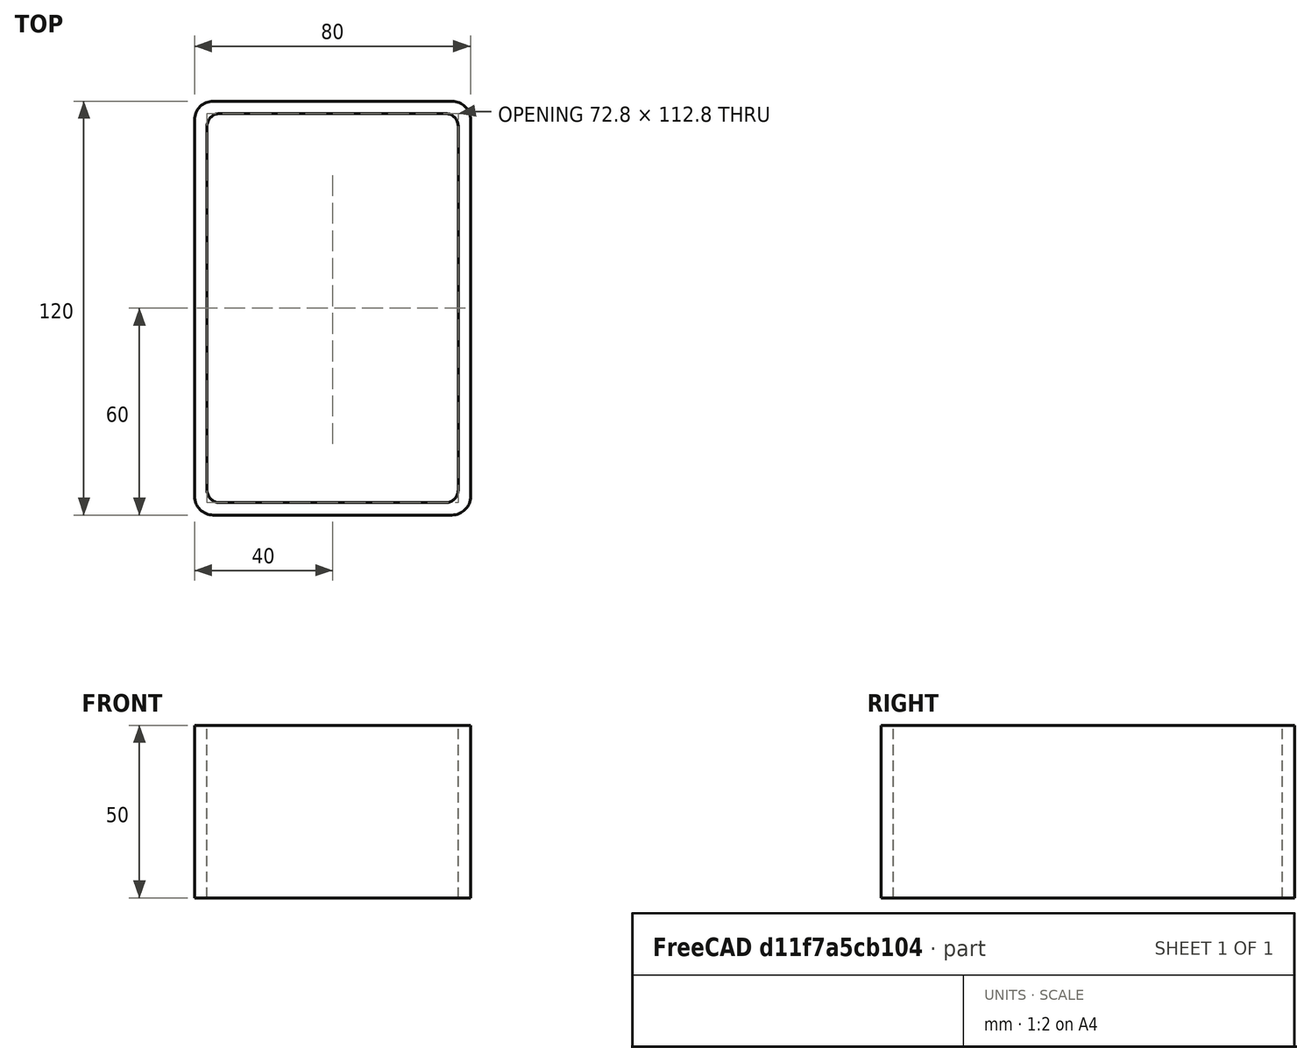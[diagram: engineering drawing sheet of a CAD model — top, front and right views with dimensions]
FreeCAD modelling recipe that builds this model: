
FCSTD DOCUMENT  (FreeCAD 0.15R4671 (Git))
Label: Rectangular hollow section 120x80x3.6 EN10219 S235JRH
License: All rights reserved
LicenseURL: http://en.wikipedia.org/wiki/All_rights_reserved
objects: Sketcher::SketchObject×1, Part::Extrusion×1
note: 2 computed .brp shape members not serialized (recipe doc carries the construction recipe); baked Part::Feature solids carry a one-line shape summary decoded from their .brp

FEATURE [Sketcher::SketchObject] Sketch
  sketch-geometry (16):
    g0: LineSegment StartX=-32.8 StartY=56.4 StartZ=0 EndX=32.8 EndY=56.4 EndZ=0
    g1: LineSegment StartX=36.4 StartY=52.8 StartZ=0 EndX=36.4 EndY=-52.8 EndZ=0
    g2: LineSegment StartX=32.8 StartY=-56.4 StartZ=0 EndX=-32.8 EndY=-56.4 EndZ=0
    g3: LineSegment StartX=-36.4 StartY=-52.8 StartZ=0 EndX=-36.4 EndY=52.8 EndZ=0
    g4: LineSegment StartX=-34.6 StartY=60 StartZ=0 EndX=34.6 EndY=60 EndZ=0
    g5: LineSegment StartX=40 StartY=54.6 StartZ=0 EndX=40 EndY=-54.6 EndZ=0
    g6: LineSegment StartX=34.6 StartY=-60 StartZ=0 EndX=-34.6 EndY=-60 EndZ=0
    g7: LineSegment StartX=-40 StartY=-54.6 StartZ=0 EndX=-40 EndY=54.6 EndZ=0
    g8: ArcOfCircle CenterX=-32.8 CenterY=52.8 CenterZ=0 NormalX=0 NormalY=0 NormalZ=1 Radius=3.6 StartAngle=1.5708 EndAngle=3.14159
    g9: ArcOfCircle CenterX=32.8 CenterY=52.8 CenterZ=0 NormalX=0 NormalY=0 NormalZ=1 Radius=3.6 StartAngle=0 EndAngle=1.5708
    g10: ArcOfCircle CenterX=32.8 CenterY=-52.8 CenterZ=0 NormalX=0 NormalY=0 NormalZ=1 Radius=3.6 StartAngle=4.71239 EndAngle=6.28319
    g11: ArcOfCircle CenterX=-32.8 CenterY=-52.8 CenterZ=0 NormalX=0 NormalY=0 NormalZ=1 Radius=3.6 StartAngle=3.14159 EndAngle=4.71239
    g12: ArcOfCircle CenterX=34.6 CenterY=54.6 CenterZ=0 NormalX=0 NormalY=0 NormalZ=1 Radius=5.4 StartAngle=0 EndAngle=1.5708
    g13: ArcOfCircle CenterX=34.6 CenterY=-54.6 CenterZ=0 NormalX=0 NormalY=0 NormalZ=1 Radius=5.4 StartAngle=4.71239 EndAngle=6.28319
    g14: ArcOfCircle CenterX=-34.6 CenterY=-54.6 CenterZ=0 NormalX=0 NormalY=0 NormalZ=1 Radius=5.4 StartAngle=3.14159 EndAngle=4.71239
    g15: ArcOfCircle CenterX=-34.6 CenterY=54.6 CenterZ=0 NormalX=0 NormalY=0 NormalZ=1 Radius=5.4 StartAngle=1.5708 EndAngle=3.14159
  constraints (36):
    c: Horizontal(g2)
    c: Vertical(g3)
    c: Horizontal(g6)
    c: Vertical(g7)
    c: Tangent(g3,g8) = 1.5708
    c: Tangent(g0,g8) = 1.5708
    c: Tangent(g0,g9) = 1.5708
    c: Tangent(g1,g9) = 1.5708
    c: Tangent(g1,g10) = 1.5708
    c: Tangent(g2,g10) = 1.5708
    c: Tangent(g2,g11) = 1.5708
    c: Tangent(g3,g11) = 1.5708
    c: Tangent(g4,g12) = 1.5708
    c: Tangent(g5,g12) = 1.5708
    c: Tangent(g5,g13) = 1.5708
    c: Tangent(g6,g13) = 1.5708
    c: Tangent(g6,g14) = 1.5708
    c: Tangent(g7,g14) = 1.5708
    c: Tangent(g7,g15) = 1.5708
    c: Tangent(g4,g15) = 1.5708
    c: Equal(g9,g8)
    c: Equal(g9,g11)
    c: Equal(g9,g10)
    c: Equal(g12,g15)
    c: Equal(g12,g14)
    c: Equal(g12,g13)
    c: Symmetric(g4,g6,g-1)
    c: Symmetric(g7,g5,g-2)
    c: DistanceY(g4,g6) = -120
    c: DistanceX(g7,g5) = 80
    c: Symmetric(g3,g1,g-2)
    c: Symmetric(g0,g2,g-1)
    c: DistanceY(g0,g4) = 3.6
    c: DistanceX(g5,g1) = -3.6
    c: Radius(g9) = 3.6
    c: Radius(g12) = 5.4
FEATURE [Part::Extrusion] Extrude  label="Rectangular hollow section 120x80x3.6 EN10219 S235JRH"
  Base = -> Sketch
  Dir = (0,0,50)
  Solid = true
